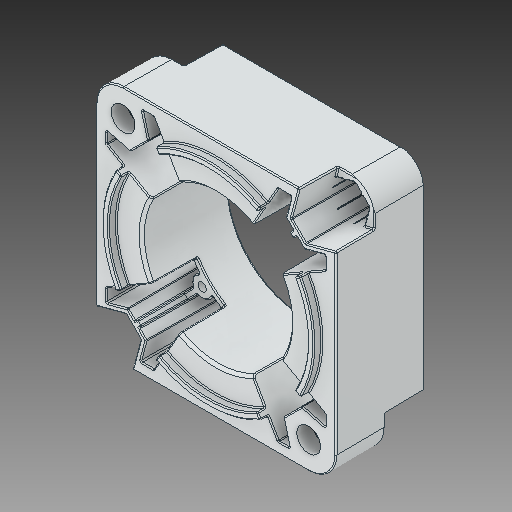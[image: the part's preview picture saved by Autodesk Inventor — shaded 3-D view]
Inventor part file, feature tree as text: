
AUTODESK INVENTOR PART (.ipt)
format: ipt  version: 2018 (Build 220112000, 112)  size: 1,586,688 bytes
history: native  units: in
note: dims shown in document units (in); Inventor stores cm internally (conversion verified against a paired STEP export)
features: chamfer x1
ambient origin geometry x8: Origin, YZ Plane, XZ Plane, XY Plane, X Axis, Y Axis, Z Axis, Center Point
bodies: Solid1 (feature_tree)
feature tree (1):
  chamfer  "Chamfer2"  [1 undecoded]
note: 1 required parameter value undecoded (feature->parameter linkage not recoverable at this tier; creation-order binding heuristic only, values carry confidence <= 0.55)
